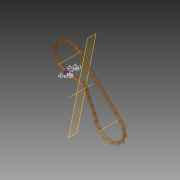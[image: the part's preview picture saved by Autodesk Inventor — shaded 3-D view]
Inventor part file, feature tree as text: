
AUTODESK INVENTOR PART (.ipt)
format: ipt  version: 2014 SP1 (Build 180222100, 222)  size: 198,144 bytes
history: native  units: mm (DEFAULTED — no unit token found)
features: other x38, extrude x33, sketch x2, plane x1, pattern_linear x1
ambient origin geometry x8: Origin, YZ Plane, XZ Plane, XY Plane, X Axis, Y Axis, Z Axis, Center Point
bodies: Body1 (feature_tree), Body2 (feature_tree), Body3 (feature_tree), Body4 (feature_tree), Body5 (feature_tree), Body6 (feature_tree), Body7 (feature_tree), Body8 (feature_tree), Body9 (feature_tree), Body10 (feature_tree), Body11 (feature_tree), Body12 (feature_tree), Body13 (feature_tree), Body14 (feature_tree), Body15 (feature_tree), Body16 (feature_tree), Body17 (feature_tree), Body18 (feature_tree), Body19 (feature_tree), Body20 (feature_tree), Body21 (feature_tree), Body22 (feature_tree), Body23 (feature_tree), Body24 (feature_tree), Body25 (feature_tree), Body26 (feature_tree), Body27 (feature_tree), Body28 (feature_tree), Body29 (feature_tree), Body30 (feature_tree), Body31 (feature_tree), Body32 (feature_tree), Body33 (feature_tree)
feature tree (75):
  sketch  "Sketch Path"  dims[d1=10.6172mm d2=7.9375mm d3=2.682204mm d5=6.981317mm d7=0.0mm d9=0.0mm d10=0.0mm d11=0.0mm d16=12.7mm d17=0.0mm d18=330.0mm]
  other  "Cross Section Plane"
  other  "Work Axis2"
  other  "Work Axis3"
  other  "Work Axis4"
  other  "Cross Section"
  plane  "Work Plane3"
  pattern_linear  "Rectangular Pattern2"  Spacing1=7.9375mm  [1 undecoded]
  sketch  "Sketch4"  dims[d0=0.0mm]
  other  "Srf41"
  other  "Srf42"
  other  "Srf43"
  other  "Srf44"
  other  "Srf45"
  other  "Srf46"
  other  "Srf47"
  other  "Srf48"
  other  "Srf49"
  other  "Srf50"
  other  "Srf51"
  other  "Srf52"
  other  "Srf53"
  other  "Srf54"
  other  "Srf55"
  other  "Srf56"
  other  "Srf57"
  other  "Srf58"
  other  "Srf59"
  other  "Srf60"
  other  "Srf61"
  other  "Srf62"
  other  "Srf63"
  other  "Srf64"
  other  "Srf65"
  other  "Srf66"
  other  "Srf67"
  other  "Srf68"
  other  "Srf69"
  other  "Srf70"
  other  "Srf71"
  other  "Srf72"
  other  "Srf73"
  extrude  "ExtrusionSrf41"  Depth=2.682204mm
  extrude  "ExtrusionSrf42"  Depth=6.981317mm
  extrude  "ExtrusionSrf43"  TaperAngle=0.0deg  [1 undecoded]
  extrude  "ExtrusionSrf44"  Depth=12.7mm TaperAngle=0.0deg
  extrude  "ExtrusionSrf45"  Depth=330.0mm
  extrude  "ExtrusionSrf46"  [1 undecoded]
  extrude  "ExtrusionSrf47"  [1 undecoded]
  extrude  "ExtrusionSrf48"  [1 undecoded]
  extrude  "ExtrusionSrf49"  [1 undecoded]
  extrude  "ExtrusionSrf50"  [1 undecoded]
  extrude  "ExtrusionSrf51"  [1 undecoded]
  extrude  "ExtrusionSrf52"  [1 undecoded]
  extrude  "ExtrusionSrf53"  [1 undecoded]
  extrude  "ExtrusionSrf54"  [1 undecoded]
  extrude  "ExtrusionSrf55"  [1 undecoded]
  extrude  "ExtrusionSrf56"  [1 undecoded]
  extrude  "ExtrusionSrf57"  [1 undecoded]
  extrude  "ExtrusionSrf58"  [1 undecoded]
  extrude  "ExtrusionSrf59"  [1 undecoded]
  extrude  "ExtrusionSrf60"  [1 undecoded]
  extrude  "ExtrusionSrf61"  [1 undecoded]
  extrude  "ExtrusionSrf62"  [1 undecoded]
  extrude  "ExtrusionSrf63"  [1 undecoded]
  extrude  "ExtrusionSrf64"  [1 undecoded]
  extrude  "ExtrusionSrf65"  [1 undecoded]
  extrude  "ExtrusionSrf66"  [1 undecoded]
  extrude  "ExtrusionSrf67"  [1 undecoded]
  extrude  "ExtrusionSrf68"  [1 undecoded]
  extrude  "ExtrusionSrf69"  [1 undecoded]
  extrude  "ExtrusionSrf70"  [1 undecoded]
  extrude  "ExtrusionSrf71"  [1 undecoded]
  extrude  "ExtrusionSrf72"  [1 undecoded]
  extrude  "ExtrusionSrf73"  [1 undecoded]
note: 30 required parameter values undecoded (feature->parameter linkage not recoverable at this tier; creation-order binding heuristic only, values carry confidence <= 0.55)
